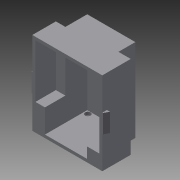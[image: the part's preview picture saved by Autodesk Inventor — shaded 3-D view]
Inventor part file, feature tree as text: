
AUTODESK INVENTOR PART (.ipt)
format: ipt  version: 2013 (Build 170138000, 138)  size: 185,344 bytes
history: native  units: mm
features: extrude x11, sketch x11, shell x1
ambient origin geometry x8: Origin, YZ Plane, XZ Plane, XY Plane, X Axis, Y Axis, Z Axis, Center Point
bodies: Solid1 (feature_tree)
feature tree (23):
  extrude  "Extrusion1"  Depth=18.5mm
  shell  "Shell1"  Thickness=8.0mm
  extrude  "Extrusion2"  Depth=31.3mm
  extrude  "Extrusion3"  Depth=6.2mm
  extrude  "Extrusion4"  Depth=2.0mm
  extrude  "Extrusion5"  Depth=7.0mm TaperAngle=0.0deg
  extrude  "Extrusion6"  Depth=2.0mm TaperAngle=0.0deg
  extrude  "Extrusion7"  Depth=54.0mm
  extrude  "Extrusion8"  Depth=21.0mm
  extrude  "Extrusion9"  Depth=2.0mm
  extrude  "Extrusion10"  Depth=19.25mm TaperAngle=0.0deg
  extrude  "Extrusion11"  Depth=34.5mm TaperAngle=0.0deg
  sketch  "Sketch1"  dims[d0=45.5mm d1=18.5mm d2=8.0mm]
  sketch  "Sketch2"  dims[d3=11.0mm d4=31.3mm]
  sketch  "Sketch3"  dims[d5=14.2mm d6=6.2mm]
  sketch  "Sketch4"  dims[d7=52.0mm d8=0.0mm d9=2.0mm]
  sketch  "Sketch5"  dims[d10=15.3mm d11=0.0mm d12=7.0mm d13=0.0mm]
  sketch  "Sketch6"  dims[d14=151.0mm d15=0.0mm d16=2.0mm d17=0.0mm]
  sketch  "Sketch7"  dims[d18=2.0mm d19=0.0mm d20=54.0mm]
  sketch  "Sketch8"  dims[d21=12.0mm d22=21.0mm]
  sketch  "Sketch9"  dims[d23=2.0mm d24=0.0mm d25=2.0mm]
  sketch  "Sketch10"  dims[d26=3.0mm d27=0.0mm d28=19.25mm d29=0.0mm]
  sketch  "Sketch11"  dims[d30=0.454mm d31=34.5mm d32=0.0mm d33=27.25mm d34=0.0mm]
